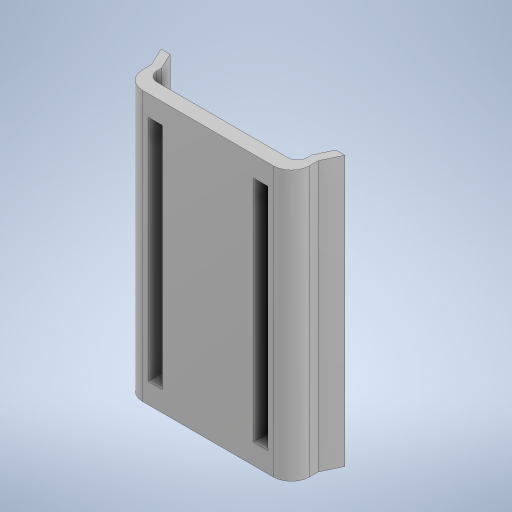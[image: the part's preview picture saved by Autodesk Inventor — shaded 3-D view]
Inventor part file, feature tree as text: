
AUTODESK INVENTOR PART (.ipt)
format: ipt  version: 2023 (Build 270158030, 158C)  size: 1,327,104 bytes
history: mixed  units: in
note: dims shown in document units (in); Inventor stores cm internally (conversion verified against a paired STEP export)
features: other x43, move_body x17, direct_edit x5, sketch x2, extrude x1, imported_body x1
ambient origin geometry x8: Origin, YZ Plane, XZ Plane, XY Plane, X Axis, Y Axis, Z Axis, Center Point
bodies: Solid1 (imported_parasolid), Solid2 (imported_parasolid), Solid3 (imported_parasolid), Solid4 (imported_parasolid), Solid5 (imported_parasolid), Solid6 (imported_parasolid), Solid7 (imported_parasolid), Solid8 (imported_parasolid), Solid9 (imported_parasolid), Solid10 (imported_parasolid), Solid11 (imported_parasolid), Solid12 (imported_parasolid), Solid13 (imported_parasolid), Solid14 (imported_parasolid), Solid15 (imported_parasolid), Solid16 (imported_parasolid), Solid17 (imported_parasolid), Solid18 (imported_parasolid), Solid19 (imported_parasolid), Solid20 (imported_parasolid), Solid21 (imported_parasolid), Solid22 (imported_parasolid), Solid23 (imported_parasolid), Solid24 (imported_parasolid), Solid25 (imported_parasolid), Solid26 (imported_parasolid), Solid27 (imported_parasolid), Solid28 (imported_parasolid), Solid29 (imported_parasolid), Solid30 (imported_parasolid), Solid31 (imported_parasolid), Solid32 (imported_parasolid), Solid33 (imported_parasolid), Solid34 (imported_parasolid), Solid35 (imported_parasolid), Solid36 (imported_parasolid), Solid37 (imported_parasolid), Solid38 (imported_parasolid), Solid39 (imported_parasolid), Solid40 (imported_parasolid), Solid41 (imported_parasolid), Solid42 (imported_parasolid), Solid43 (imported_parasolid)
feature tree (69):
  direct_edit  "Direct Edit1"
  direct_edit  "Direct Edit2"
  direct_edit  "Direct Edit3"
  direct_edit  "Direct Edit4"
  sketch  "Sketch1"  dims[d0=0.0in d1=0.0in d2=-0.2559in d3=0.0in d4=0.0in d5=0.1969in]
  direct_edit  "Direct Edit5"
  extrude  "Extrusion1"  Depth=0.1969in TaperAngle=0.0deg
  sketch  "Sketch2"  dims[d6=0.0in d7=0.0in d8=0.1969in d9=0.0in d10=0.0in d11=0.0591in d12=0.0in d13=0.0in d14=-0.0256in d15=0.0in d16=0.0in d17=-0.0256in d18=0.0in d19=0.0in d20=-0.0256in d21=0.0in d22=0.0in d23=-0.0256in d24=0.0in d25=0.0in d26=-0.1969in d27=0.0in d28=0.0in d29=-0.1969in d30=0.0in d31=0.0in d32=0.0984in d33=0.0in d34=0.0in d35=0.0984in d36=0.0in d37=0.0in d38=-0.1969in d39=0.0in d40=0.0in d41=-0.1969in d42=0.0in d43=0.0in d44=0.5472in d45=0.0in d46=0.0in d47=0.8661in d48=0.1181in d50=0.1181in d51=0.2362in d52=0.3937in d53=0.0in d54=0.1181in d55=0.1575in d56=0.0in d57=0.0in d58=0.0591in d59=0.0591in]
  other  "Rat_ToothHolder"
  other  "StandExtention"
  other  "CableHolderPlate"
  other  "Mouse_ToothHolder"
  other  "Base_Joint1"
  other  "MouseEarbar"
  other  "MouseEarbar (1)"
  other  "PreampPlate"
  other  "CableHolderTop"
  other  "MouseNoseCone"
  other  "HeadFixClamp"
  other  "HEadFixBase"
  other  "HeadFixBase2"
  other  "HeadFixClamp2"
  other  "Base_Joint2"
  other  "CableHolderArm1"
  other  "CableHolderArm2"
  other  "CableHolderClamp2"
  other  "CableHolderArm4"
  other  "CableHolderArm3"
  other  "NoseConeStand (1) (2)"
  other  "PET-attach"
  other  "RatNoseCone"
  other  "Holder_For_Odor_Delivery"
  other  "MouseHeadCapBase"
  other  "MouseHeadCapBase_I"
  other  "MouseHeadCapBase_II"
  other  "MouseHeadCapBase_III"
  other  "BedTop (1)"
  other  "BedSpacer (1) (1)"
  other  "BedSpacer (2) (1)"
  other  "BedSpacer (3) (1)"
  other  "BedSpacer (4)"
  other  "BedBottom (1)"
  other  "Mouse restrainer"
  other  "Resterainer pusher"
  other  "RatEarbar_1"
  other  "RatEarbar_2"
  other  "Base_Joint1 (1) (1)"
  other  "Base_Joint1 (1) (1) (1)"
  other  "Base_Joint1 (1)"
  other  "Base (1) (1)"
  other  "Base_Joint2 (1)"
  move_body  "Move1"
  move_body  "Move2"
  move_body  "Move3"
  move_body  "Move4"
  move_body  "Move5"
  move_body  "Move6"
  move_body  "Move7"
  move_body  "Move8"
  move_body  "Move9"
  move_body  "Move10"
  move_body  "Move11"
  move_body  "Move12"
  move_body  "Move13"
  move_body  "Move14"
  move_body  "Move15"
  move_body  "Move16"
  move_body  "Move17"
  imported_body  NMx_Import_Brep_tag  [imported B-rep: ~6 faces, bbox_mm=None]
